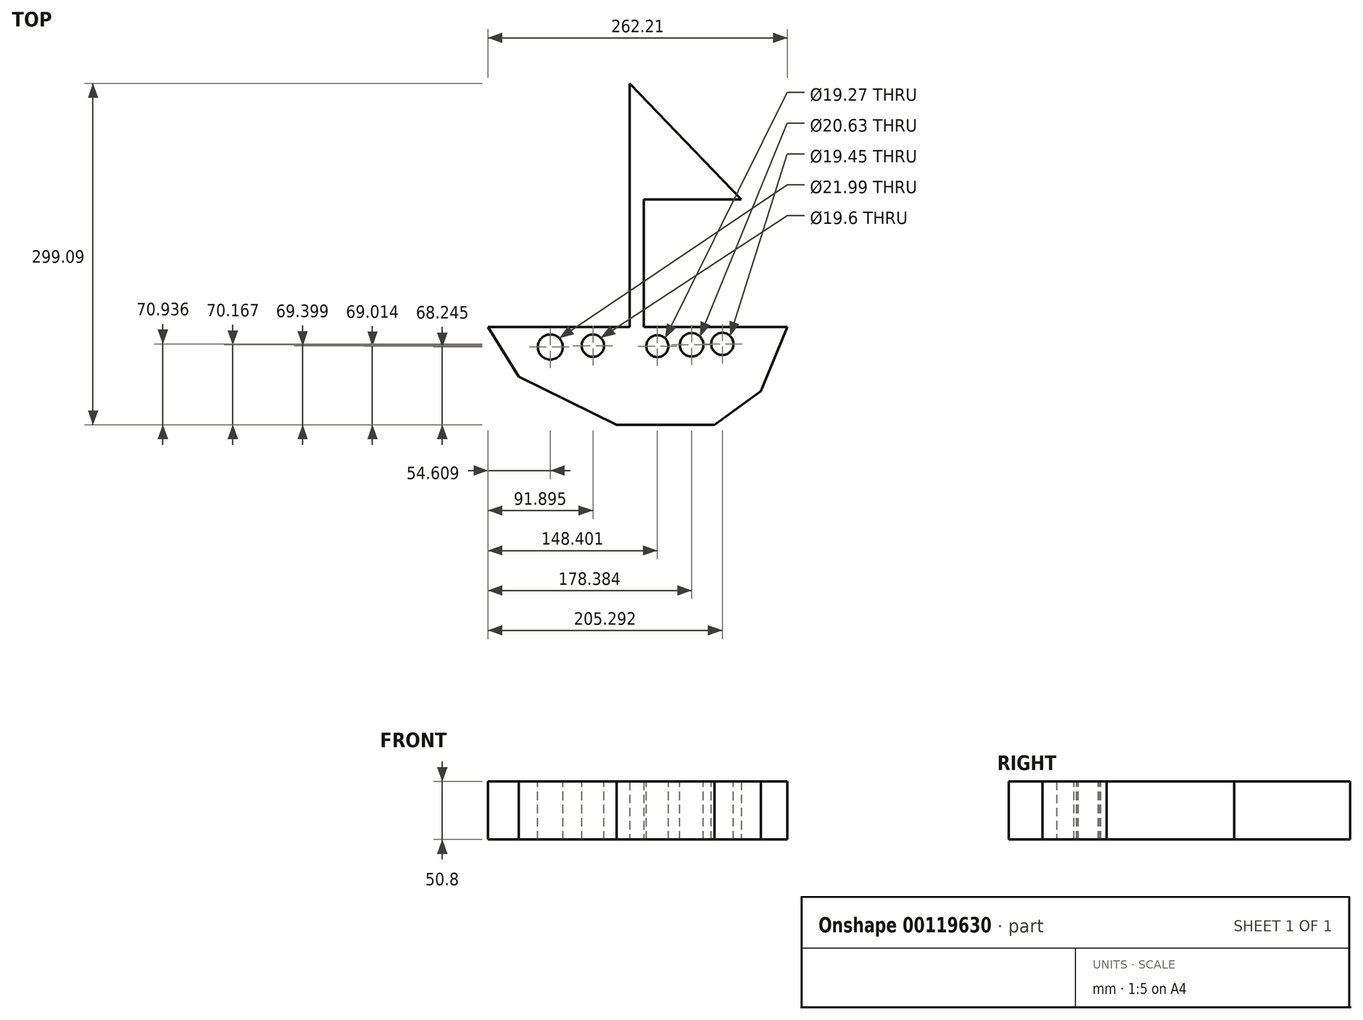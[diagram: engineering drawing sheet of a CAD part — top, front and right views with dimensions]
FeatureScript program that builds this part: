
annotation { "Feature Type Name" : "Feature", "Feature Type Description" : "" }
export const myFeature = defineFeature(function(context is Context, id is Id, definition is map)
    precondition{}
    {
        {
            var Q0;
            Q0=qCreatedBy(makeId("Top.planeOp"),FACE);
            var sketch = newSketch(context, id + "F0", { "sketchPlane" : qUnion([Q0])});
            skLineSegment(sketch, "E0", {"start": v(0, 0) * mm, "end": v(0, 213.36) * mm});
            skLineSegment(sketch, "E1", {"start": v(0, 213.36) * mm, "end": v(97.83, 111.9) * mm});
            skLineSegment(sketch, "E2", {"start": v(97.83, 111.9) * mm, "end": v(0, 111.9) * mm});
            skLineSegment(sketch, "E3", {"start": v(0, 111.9) * mm, "end": v(0, 0) * mm});
            skLineSegment(sketch, "E4", {"start": v(138.02, 0) * mm, "end": v(0, 0) * mm});
            skLineSegment(sketch, "E5", {"start": v(0, 0) * mm, "end": v(-124.19, 0) * mm});
            skLineSegment(sketch, "E6", {"start": v(-124.19, 0) * mm, "end": v(-97.18, -43.57) * mm});
            skLineSegment(sketch, "E7", {"start": v(-97.18, -43.57) * mm, "end": v(-11.53, -85.73) * mm});
            skLineSegment(sketch, "E8", {"start": v(-11.53, -85.73) * mm, "end": v(74.11, -85.73) * mm});
            skLineSegment(sketch, "E9", {"start": v(74.11, -85.73) * mm, "end": v(114.96, -56.09) * mm});
            skLineSegment(sketch, "E10", {"start": v(114.96, -56.09) * mm, "end": v(138.02, 0) * mm});
            skLineSegment(sketch, "E11", {"start": v(12.3, 111.9) * mm, "end": v(12.3, 0) * mm});
            skSolve(sketch);
        }
        {
            var Q0;
            Q0 = qSketchRegion(id + "F0", true);
            extrude(context, id + "F1", {"entities" : qUnion([Q0]), "depth" : 25.4 * mm});
        }
        {
            var Q0;
            Q0 = qSketchRegion(id + "F0", true);
            extrude(context, id + "F2", {"entities" : qUnion([Q0]), "operationType" : NewBodyOperationType.ADD, "depth" : 50.8 * mm});
        }
        {
            var Q0;
            Q0=makeQuery(id+"F2.opExtrude","CAP_FACE",FACE,{"disambiguationData":[OSD([sQuery(id+"F0.wireOp",EDGE,"E0"),sQuery(id+"F0.wireOp",EDGE,"E1"),sQuery(id+"F0.wireOp",EDGE,"E2"),sQuery(id+"F0.wireOp",EDGE,"E3"),sQuery(id+"F0.wireOp",EDGE,"E4"),sQuery(id+"F0.wireOp",EDGE,"E5"),sQuery(id+"F0.wireOp",EDGE,"E6"),sQuery(id+"F0.wireOp",EDGE,"E7"),sQuery(id+"F0.wireOp",EDGE,"E8"),sQuery(id+"F0.wireOp",EDGE,"E9"),sQuery(id+"F0.wireOp",EDGE,"E10"),sQuery(id+"F0.wireOp",EDGE,"E11")])],"isStart":false});
            var sketch = newSketch(context, id + "F3", { "sketchPlane" : qUnion([Q0])});
            skCircle(sketch, "E12", {"center": v(-69.58, -17.48) * mm, "radius": 11 * mm});
            skCircle(sketch, "E13", {"center": v(-32.3, -16.33) * mm, "radius": 9.8 * mm});
            skCircle(sketch, "E14", {"center": v(24.21, -16.72) * mm, "radius": 9.63 * mm});
            skCircle(sketch, "E15", {"center": v(54.2, -15.56) * mm, "radius": 10.31 * mm});
            skCircle(sketch, "E16", {"center": v(81.1, -14.8) * mm, "radius": 9.72 * mm});
            skSolve(sketch);
        }
        {
            var Q0;
            Q0=makeQuery(id+"F3.imprint","IMPRINT",FACE,{"disambiguationData":[TD([[makeQuery(id+"F3.imprint","IMPRINT",EDGE,{"derivedFrom":sQuery(id+"F3.wireOp",EDGE,"E14")}),1.0]])]});
            var Q1;
            Q1=makeQuery(id+"F3.imprint","IMPRINT",FACE,{"disambiguationData":[TD([[makeQuery(id+"F3.imprint","IMPRINT",EDGE,{"derivedFrom":sQuery(id+"F3.wireOp",EDGE,"E15")}),1.0]])]});
            var Q2;
            Q2=makeQuery(id+"F3.imprint","IMPRINT",FACE,{"disambiguationData":[TD([[makeQuery(id+"F3.imprint","IMPRINT",EDGE,{"derivedFrom":sQuery(id+"F3.wireOp",EDGE,"E16")}),1.0]])]});
            var Q3;
            Q3=makeQuery(id+"F3.imprint","IMPRINT",FACE,{"disambiguationData":[TD([[makeQuery(id+"F3.imprint","IMPRINT",EDGE,{"derivedFrom":sQuery(id+"F3.wireOp",EDGE,"E12")}),1.0]])]});
            var Q4;
            Q4=makeQuery(id+"F3.imprint","IMPRINT",FACE,{"disambiguationData":[TD([[makeQuery(id+"F3.imprint","IMPRINT",EDGE,{"derivedFrom":sQuery(id+"F3.wireOp",EDGE,"E13")}),1.0]])]});
            extrude(context, id + "F4", {"entities" : qUnion([Q0, Q1, Q2, Q3, Q4]), "operationType" : NewBodyOperationType.REMOVE, "oppositeDirection" : true, "depth" : 50.8 * mm});
        }
    });
